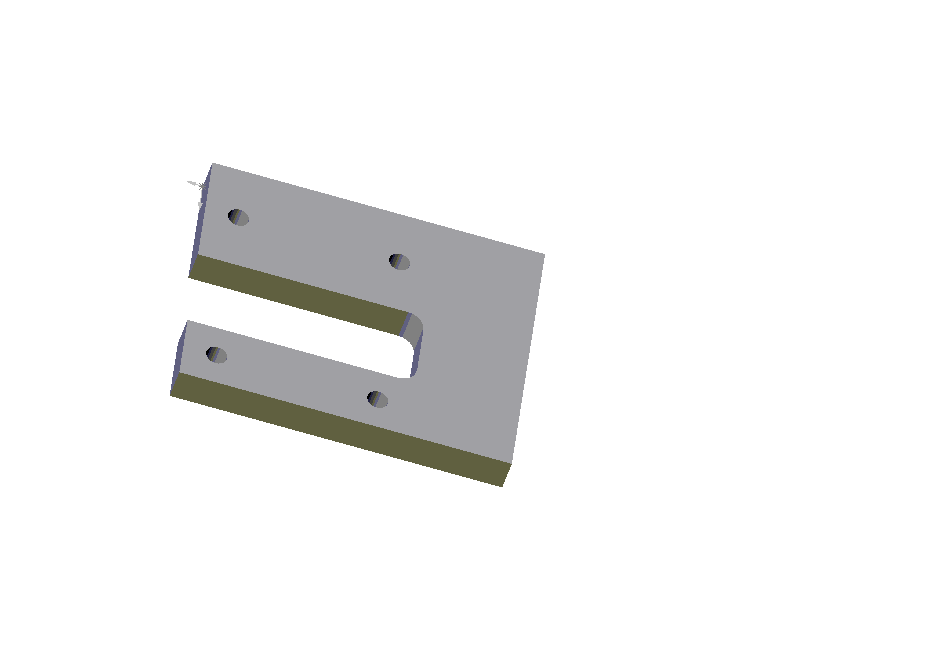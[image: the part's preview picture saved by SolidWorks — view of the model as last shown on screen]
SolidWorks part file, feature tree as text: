
SOLIDWORKS PART (.sldprt)
format: sldprt  version: not decoded by parser v0  size: 166,400 bytes
history: native  units: mm
features: sketch x173, plane x3, extrude x1 + 2 further entries (+5 scaffold rows collapsed; 18 parser-record rows omitted)
feature tree (202):
  scaffold x5  (default folders/planes/origin — collapsed)
  plane  "Plane1"
  plane  "Plane2"
  plane  "Plane3"
  sketch  "Sketch1"  dims[c1.D6=10.0mm c2.D6=10.0mm c2.D7=6.0mm c2.D10=5.0mm c2.D1=20.0mm c2.D2=35.0mm c2.D3=25.0mm c2.D4=95.0mm c2.D5=65.0mm c3.D6=17.5mm c3.D7=23.0mm c3.D8=10.0mm c3.D9=23.0mm]
  extrude  "Base-Extrude"  Depth=10mm cosMaterialEX=8300000000.0
  sketch  "cosMaterialNUXY"
  sketch  "cosMaterialGXY"
  sketch  "cosMaterialALPX"
  sketch  "cosMaterialDENS"
  sketch  "cosMaterialKX"
  sketch  "cosMaterialC"
  sketch  "Units"
  sketch  "AnalysisType"
  sketch  "MeshType"
  sketch  "cosMaterialSIGYLD"
  sketch  "cosMaterialSIGXT"
  sketch  "cosMaterialSIGXC"  dims[sMaterialName=0.0mm cosFMVItemName=0.0mm cosMaterialName=0.0mm cosComponentName=0.0mm]
  sketch  "cosMaterialEX"
  sketch  "cosMaterialNUXY"
  sketch  "cosMaterialGXY"
  sketch  "cosMaterialALPX"
  sketch  "cosMaterialDENS"
  sketch  "cosMaterialKX"
  sketch  "cosMaterialC"
  sketch  "Units"
  sketch  "AnalysisType"
  sketch  "MeshType"
  sketch  "cosMaterialSIGYLD"
  sketch  "cosMaterialSIGXT"
  sketch  "cosMaterialSIGXC"  dims[sMaterialSourceName=0.0mm sMaterialName=0.0mm cosFMVItemName=0.0mm cosMaterialName=0.0mm cosComponentName=0.0mm]
  "base_curta:Restraint-1"
  sketch  "RestraintType"
  sketch  "Value"
  sketch  "cosRestraintComp:1"
  sketch  "cosRestraintComp:2"
  sketch  "cosRestraintComp:3"
  sketch  "cosRestraintComp:4"
  sketch  "cosRestraintComp:5"
  sketch  "cosRestraintComp:6"
  sketch  "Unit"
  sketch  "AnalysisType"
  sketch  "MeshType"
  sketch  "cosRestraintCompCheck1"
  sketch  "cosRestraintCompCheck2"
  sketch  "cosRestraintCompCheck3"
  sketch  "cosRestraintCompCheck4"
  sketch  "cosRestraintCompCheck5"
  sketch  "cosRestraintCompCheck6"
  sketch  "cosRestraintRefPlaneSet"
  sketch  "cosRestraintRefPlaneOrigin1"
  sketch  "cosRestraintRefPlaneOrigin2"
  sketch  "cosRestraintRefPlaneOrigin3"
  sketch  "cosRestraintRefPlaneXDir1"
  sketch  "cosRestraintRefPlaneXDir2"
  sketch  "cosRestraintRefPlaneXDir3"
  sketch  "cosRestraintRefPlaneNormal1"
  sketch  "cosRestraintRefPlaneNormal2"
  sketch  "cosRestraintRefPlaneNormal3"  dims[cosRestraintRefPlaneName=0.0mm]
  sketch  "cosRestraintCoordSystemType"
  sketch  "cosRestraintFaceTypeMask"  dims[cosFMVItemName=0.0mm cosRestraint4=0.0]
  sketch  "RestraintType"
  sketch  "Value"
  sketch  "cosRestraintComp:1"
  sketch  "cosRestraintComp:2"
  sketch  "cosRestraintComp:3"
  sketch  "cosRestraintComp:4"
  sketch  "cosRestraintComp:5"
  sketch  "cosRestraintComp:6"
  sketch  "Unit"
  sketch  "AnalysisType"
  sketch  "MeshType"
  sketch  "cosRestraintCompCheck1"
  sketch  "cosRestraintCompCheck2"
  sketch  "cosRestraintCompCheck3"
  sketch  "cosRestraintCompCheck4"
  sketch  "cosRestraintCompCheck5"
  sketch  "cosRestraintCompCheck6"
  sketch  "cosRestraintRefPlaneSet"
  sketch  "cosRestraintRefPlaneOrigin1"
  sketch  "cosRestraintRefPlaneOrigin2"
  sketch  "cosRestraintRefPlaneOrigin3"
  sketch  "cosRestraintRefPlaneXDir1"
  sketch  "cosRestraintRefPlaneXDir2"
  sketch  "cosRestraintRefPlaneXDir3"
  sketch  "cosRestraintRefPlaneNormal1"
  sketch  "cosRestraintRefPlaneNormal2"
  sketch  "cosRestraintRefPlaneNormal3"  dims[cosRestraintRefPlaneName=0.0mm]
  sketch  "cosRestraintCoordSystemType"
  sketch  "cosRestraintFaceTypeMask"  dims[cosFMVItemName=0.0mm]
  "base_curta:Force-1"
  sketch  "cosForceComp:1"
  sketch  "cosForceComp:2"
  sketch  "cosForceComp:3"
  sketch  "cosForceComp:4"
  sketch  "cosForceComp:5"
  sketch  "cosForceComp:6"
  sketch  "cosForceTorqueNF"
  sketch  "cosForceCompCheck1"
  sketch  "cosForceCompCheck2"
  sketch  "cosForceCompCheck3"
  sketch  "cosForceCompCheck4"
  sketch  "cosForceCompCheck5"
  sketch  "cosForceCompCheck6"
  sketch  "Unit"
  sketch  "AnalysisType"
  sketch  "MeshType"
  sketch  "cosForceRefPlaneSet"
  sketch  "cosForceRefPlaneOrigin1"
  sketch  "cosForceRefPlaneOrigin2"
  sketch  "cosForceRefPlaneOrigin3"
  sketch  "cosForceRefPlaneXDir1"
  sketch  "cosForceRefPlaneXDir2"
  sketch  "cosForceRefPlaneXDir3"
  sketch  "cosForceRefPlaneNormal1"
  sketch  "cosForceRefPlaneNormal2"
  sketch  "cosForceRefPlaneNormal3"  dims[cosForceRefPlaneName=0.0mm]
  sketch  "cosForceCoordSystemType"
  sketch  "cosForceType"  dims[cosFMVItemName=0.0mm]
  sketch  "cosDistributionType"  dims[cosDistributionCoordSysName=0.0mm]
  sketch  "cosDistributionCoef1"
  sketch  "cosDistributionCoef2"
  sketch  "cosDistributionCoef3"
  sketch  "cosDistributionCoef4"
  sketch  "cosDistributionCoef5"
  sketch  "cosDistributionCoef6"  dims[cosForce5=0.0]
  sketch  "cosForceComp:1"
  sketch  "cosForceComp:2"
  sketch  "cosForceComp:3"
  sketch  "cosForceComp:4"
  sketch  "cosForceComp:5"
  sketch  "cosForceComp:6"
  sketch  "cosForceTorqueNF"
  sketch  "cosForceCompCheck1"
  sketch  "cosForceCompCheck2"
  sketch  "cosForceCompCheck3"
  sketch  "cosForceCompCheck4"
  sketch  "cosForceCompCheck5"
  sketch  "cosForceCompCheck6"
  sketch  "Unit"
  sketch  "AnalysisType"
  sketch  "MeshType"
  sketch  "cosForceRefPlaneSet"
  sketch  "cosForceRefPlaneOrigin1"
  sketch  "cosForceRefPlaneOrigin2"
  sketch  "cosForceRefPlaneOrigin3"
  sketch  "cosForceRefPlaneXDir1"
  sketch  "cosForceRefPlaneXDir2"
  sketch  "cosForceRefPlaneXDir3"
  sketch  "cosForceRefPlaneNormal1"
  sketch  "cosForceRefPlaneNormal2"
  sketch  "cosForceRefPlaneNormal3"  dims[cosForceRefPlaneName=0.0mm]
  sketch  "cosForceCoordSystemType"
  sketch  "cosForceType"  dims[cosFMVItemName=0.0mm]
  sketch  "cosDistributionType"  dims[cosDistributionCoordSysName=0.0mm]
  sketch  "cosDistributionCoef1"
  sketch  "cosDistributionCoef2"
  sketch  "cosDistributionCoef3"
  sketch  "cosDistributionCoef4"
  sketch  "cosDistributionCoef5"
  sketch  "cosDistributionCoef6"
  parser-record x18  (decoder bookkeeping rows leaked as tree rows — omitted from the tree; the rows remain in map.json)
  sketch  "faceID"  dims[cosFaceID=0.0]
  sketch  "faceID"
  sketch  "faceID"
  sketch  "faceID"
  sketch  "faceID"
  sketch  "faceID"
  sketch  "faceID"
  sketch  "faceID"
  sketch  "faceID"
  sketch  "faceID"
  sketch  "faceID"
  sketch  "faceID"
  sketch  "faceID"
  sketch  "faceID"
  sketch  "faceID"
  sketch  "faceID"
  sketch  "faceID"
  sketch  "faceID"
  sketch  "faceID"
decode coverage: 16 of 174 modeling features carry decoded parameters; 2 rows unclassified (native names shown)
note: suppression state not decoded; provenance and decode notes live in map.json
